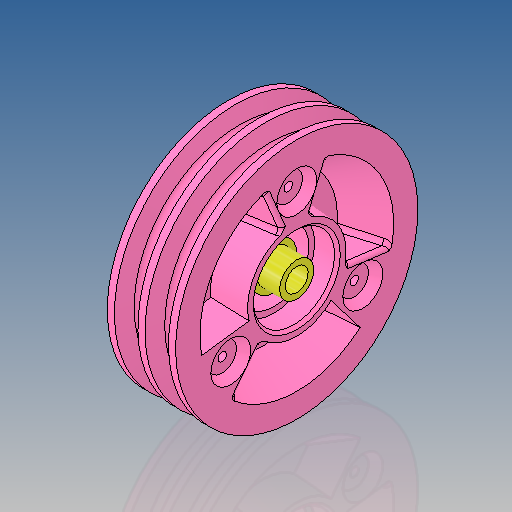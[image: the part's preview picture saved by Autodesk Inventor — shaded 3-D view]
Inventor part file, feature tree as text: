
AUTODESK INVENTOR PART (.ipt)
format: ipt  version: 2017 (Build 210142000, 142)  size: 604,160 bytes
history: native  units: mm
features: revolve x5, other x4, chamfer x4, extrude x3, sketch x2, plane x2, fillet x1, pattern_circular x1, split x1
ambient origin geometry x8: Origin, YZ Plane, XZ Plane, XY Plane, X Axis, Y Axis, Z Axis, Center Point
bodies: Body1 (feature_tree), Body2 (feature_tree), Body3 (feature_tree)
feature tree (23):
  other  "Sólido1"
  sketch  "Boceto1"  dims[d0=8.0mm d1=28.5mm]
  revolve  "Revolución1"  [1 undecoded]
  sketch  "Boceto2"  dims[d2=24.5mm d3=6.0mm d4=4.0mm d5=85.0mm d6=20.0mm d7=2.5mm d8=90.0deg d10=9.0mm d11=3.0mm d13=52.5mm d14=10.0mm d15=0.0mm d16=10.0mm d17=0.0mm d18=8.0mm d24=44.5mm d25=49.5mm d26=8.0mm d27=12.0mm d28=16.0mm d29=8.0mm d30=90.0deg d31=24.0mm d32=30.0mm d33=18.0mm d34=8.281806mm d35=3.0mm d36=0.0mm d37=60.0deg d39=1.5mm d40=30.0mm d41=360.0deg d43=60.0deg d44=1.5mm d45=90.0deg d46=1.0mm d47=2.0mm d48=45.0deg d49=2.0mm d50=3.0mm d51=45.0deg d52=4.0mm d53=70.0mm d54=3.0mm d55=90.0deg d56=120.0deg d59=12.0mm d60=2.0mm d61=17.453293mm d65=7.0mm d66=3.0mm d67=7.0mm d68=7.0mm d69=10.0mm d70=45.0deg d71=12.0mm d72=12.0mm d73=2.0mm d74=17.453293mm d75=30.0deg d76=30.0deg]
  extrude  "Extrusión1"  Depth=10.0mm
  chamfer  "Chaflán1"  Distance=4.0mm
  revolve  "Revolución6"  [1 undecoded]
  plane  "Plano de trabajo1"
  extrude  "Extrusión2"  Depth=10.0mm
  extrude  "Extrusión3"  TaperAngle=90.0deg  [1 undecoded]
  chamfer  "Chaflán2"  Distance=9.0mm
  chamfer  "Chaflán3"  Distance=3.0mm
  chamfer  "Chaflán5"  Distance=52.5mm
  fillet  "Empalme1"  Radius=10.0mm
  pattern_circular  "Patrón circular1"  [2 undecoded]
  plane  "Plano de trabajo2"
  revolve  "Revolución4"  [1 undecoded]
  revolve  "Revolución5"  [1 undecoded]
  revolve  "Revolución2"  [1 undecoded]
  split  "Dividir1"
  other  "espaciador"
  other  "Sólido3"
  other  "Sólido4"
note: 8 required parameter values undecoded (feature->parameter linkage not recoverable at this tier; creation-order binding heuristic only, values carry confidence <= 0.55)